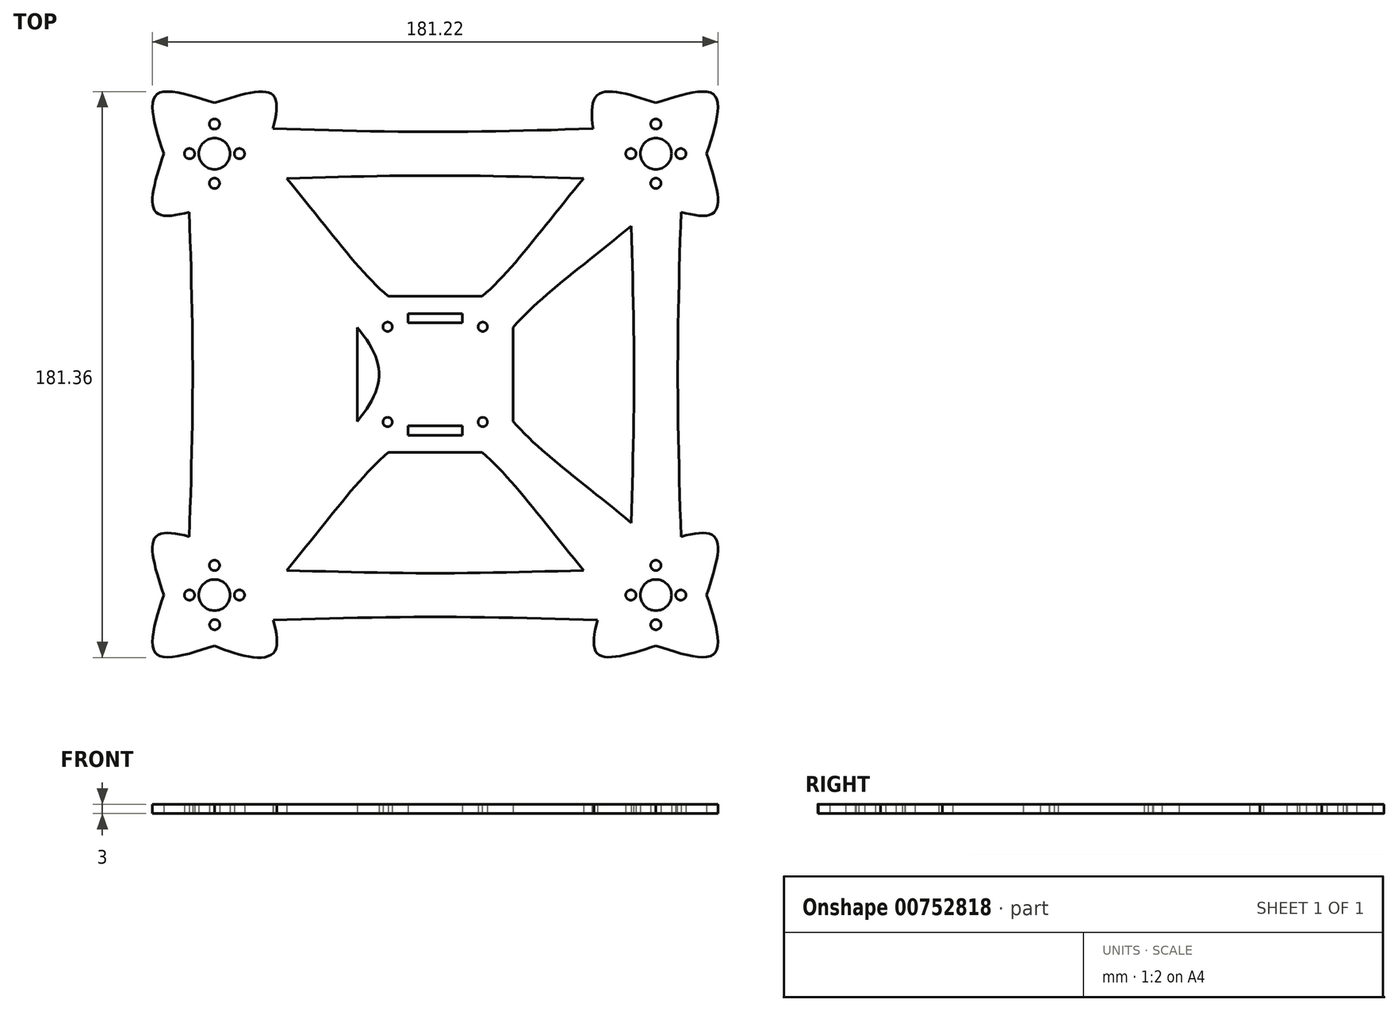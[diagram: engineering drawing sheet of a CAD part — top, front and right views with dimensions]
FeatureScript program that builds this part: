
annotation { "Feature Type Name" : "Feature", "Feature Type Description" : "" }
export const myFeature = defineFeature(function(context is Context, id is Id, definition is map)
    precondition{}
    {
        {
            var Q0;
            Q0=qCreatedBy(makeId("Top.planeOp"),FACE);
            var sketch = newSketch(context, id + "F0", { "sketchPlane" : qUnion([Q0])});
            skLineSegment(sketch, "E0.bottom", {"start": v(-18, 18) * mm, "end": v(18, 18) * mm, "construction": true});
            skLineSegment(sketch, "E0.top", {"start": v(-18, -18) * mm, "end": v(18, -18) * mm, "construction": true});
            skLineSegment(sketch, "E0.left", {"start": v(-18, 18) * mm, "end": v(-18, -18) * mm, "construction": true});
            skLineSegment(sketch, "E0.right", {"start": v(18, 18) * mm, "end": v(18, -18) * mm, "construction": true});
            skLineSegment(sketch, "E1", {"start": v(0, 18) * mm, "end": v(0, -18) * mm, "construction": true});
            skLineSegment(sketch, "E2", {"start": v(-18, 0) * mm, "end": v(18, 0) * mm, "construction": true});
            skPoint(sketch, "E3.positionSnap0", {"position": v(0, 0) * mm});
            skLineSegment(sketch, "E4", {"start": v(0, 0) * mm, "end": v(70.71, 70.71) * mm, "construction": true});
            skLineSegment(sketch, "E5", {"start": v(0, 0) * mm, "end": v(-70.71, -70.71) * mm, "construction": true});
            skLineSegment(sketch, "E6", {"start": v(0, 0) * mm, "end": v(70.71, -70.71) * mm, "construction": true});
            skCircle(sketch, "E7", {"center": v(-70.71, 70.71) * mm, "radius": 63.5 * mm, "construction": true});
            skCircle(sketch, "E8", {"center": v(70.71, 70.71) * mm, "radius": 63.5 * mm, "construction": true});
            skCircle(sketch, "E9", {"center": v(-70.71, -70.71) * mm, "radius": 63.5 * mm, "construction": true});
            skCircle(sketch, "E10", {"center": v(70.71, -70.71) * mm, "radius": 63.5 * mm, "construction": true});
            skCircle(sketch, "E11", {"center": v(-70.71, 70.71) * mm, "radius": 5 * mm});
            skCircle(sketch, "E12", {"center": v(70.71, 70.71) * mm, "radius": 5 * mm});
            skCircle(sketch, "E13", {"center": v(-70.71, -70.71) * mm, "radius": 5 * mm});
            skCircle(sketch, "E14", {"center": v(70.71, -70.71) * mm, "radius": 5 * mm});
            skLineSegment(sketch, "E15", {"start": v(-70.71, 70.71) * mm, "end": v(-62.71, 70.71) * mm, "construction": true});
            skCircle(sketch, "E16", {"center": v(-78.71, 70.71) * mm, "radius": 1.65 * mm});
            skCircle(sketch, "E17", {"center": v(-70.71, 80.21) * mm, "radius": 1.65 * mm});
            skCircle(sketch, "E18", {"center": v(-62.71, 70.71) * mm, "radius": 1.65 * mm});
            skCircle(sketch, "E19", {"center": v(-70.71, 61.21) * mm, "radius": 1.65 * mm});
            skLineSegment(sketch, "E20", {"start": v(70.71, 70.71) * mm, "end": v(62.71, 70.71) * mm, "construction": true});
            skLineSegment(sketch, "E21", {"start": v(70.71, 70.71) * mm, "end": v(78.71, 70.71) * mm, "construction": true});
            skLineSegment(sketch, "E22", {"start": v(70.71, 70.71) * mm, "end": v(70.71, 80.21) * mm, "construction": true});
            skLineSegment(sketch, "E23", {"start": v(70.71, 70.71) * mm, "end": v(70.71, 61.21) * mm, "construction": true});
            skCircle(sketch, "E24", {"center": v(62.71, 70.71) * mm, "radius": 1.65 * mm});
            skCircle(sketch, "E25", {"center": v(70.71, 80.21) * mm, "radius": 1.65 * mm});
            skCircle(sketch, "E26", {"center": v(70.71, 61.21) * mm, "radius": 1.65 * mm});
            skCircle(sketch, "E27", {"center": v(78.71, 70.71) * mm, "radius": 1.65 * mm});
            skLineSegment(sketch, "E28", {"start": v(-70.71, -70.71) * mm, "end": v(-78.71, -70.71) * mm, "construction": true});
            skLineSegment(sketch, "E29", {"start": v(-70.71, -70.71) * mm, "end": v(-62.71, -70.71) * mm, "construction": true});
            skLineSegment(sketch, "E30", {"start": v(-70.71, -70.71) * mm, "end": v(-70.71, -61.21) * mm, "construction": true});
            skLineSegment(sketch, "E31", {"start": v(-70.71, -70.71) * mm, "end": v(-70.64, -80.21) * mm, "construction": true});
            skCircle(sketch, "E32", {"center": v(-78.71, -70.71) * mm, "radius": 1.65 * mm});
            skCircle(sketch, "E33", {"center": v(-70.71, -61.21) * mm, "radius": 1.65 * mm});
            skCircle(sketch, "E34", {"center": v(-62.71, -70.71) * mm, "radius": 1.65 * mm});
            skCircle(sketch, "E35", {"center": v(-70.64, -80.21) * mm, "radius": 1.65 * mm});
            skLineSegment(sketch, "E36", {"start": v(70.71, -70.71) * mm, "end": v(78.71, -70.71) * mm, "construction": true});
            skLineSegment(sketch, "E37", {"start": v(70.71, -70.71) * mm, "end": v(62.71, -70.71) * mm, "construction": true});
            skCircle(sketch, "E38", {"center": v(62.71, -70.71) * mm, "radius": 1.65 * mm});
            skCircle(sketch, "E39", {"center": v(78.71, -70.71) * mm, "radius": 1.65 * mm});
            skLineSegment(sketch, "E40", {"start": v(70.71, -70.71) * mm, "end": v(70.71, -61.21) * mm, "construction": true});
            skLineSegment(sketch, "E41", {"start": v(70.71, -70.71) * mm, "end": v(70.71, -80.21) * mm, "construction": true});
            skCircle(sketch, "E42", {"center": v(70.71, -61.21) * mm, "radius": 1.65 * mm});
            skCircle(sketch, "E43", {"center": v(70.71, -80.21) * mm, "radius": 1.65 * mm});
            skCircle(sketch, "E44", {"center": v(-15.25, 15.25) * mm, "radius": 1.5 * mm});
            skCircle(sketch, "E45", {"center": v(15.25, 15.25) * mm, "radius": 1.5 * mm});
            skCircle(sketch, "E46", {"center": v(-15.25, -15.25) * mm, "radius": 1.5 * mm});
            skCircle(sketch, "E47", {"center": v(15.25, -15.25) * mm, "radius": 1.5 * mm});
            skLineSegment(sketch, "E48", {"start": v(-15.25, 15.25) * mm, "end": v(15.25, 15.25) * mm, "construction": true});
            skLineSegment(sketch, "E49", {"start": v(-15.25, 15.25) * mm, "end": v(-15.25, -15.25) * mm, "construction": true});
            skLineSegment(sketch, "E50", {"start": v(15.25, -15.25) * mm, "end": v(-15.25, -15.25) * mm, "construction": true});
            skLineSegment(sketch, "E51", {"start": v(15.25, 15.25) * mm, "end": v(15.25, -15.25) * mm, "construction": true});
            skCircle(sketch, "E52", {"center": v(-70.71, 70.71) * mm, "radius": 13.3 * mm, "construction": true});
            skLineSegment(sketch, "E53.bottom", {"start": v(-51.96, 89.46) * mm, "end": v(-89.46, 89.46) * mm, "construction": true});
            skLineSegment(sketch, "E53.top", {"start": v(-51.96, 51.96) * mm, "end": v(-89.46, 51.96) * mm, "construction": true});
            skLineSegment(sketch, "E53.left", {"start": v(-51.96, 89.46) * mm, "end": v(-51.96, 51.96) * mm, "construction": true});
            skLineSegment(sketch, "E53.right", {"start": v(-89.46, 89.46) * mm, "end": v(-89.46, 51.96) * mm, "construction": true});
            skLineSegment(sketch, "E54", {"start": v(-70.71, 84.01) * mm, "end": v(-70.71, 89.46) * mm, "construction": true});
            skLineSegment(sketch, "E55", {"start": v(-70.71, 89.46) * mm, "end": v(-89.46, 89.46) * mm, "construction": true});
            skLineSegment(sketch, "E56", {"start": v(-89.46, 70.71) * mm, "end": v(-89.46, 51.96) * mm, "construction": true});
            skLineSegment(sketch, "E57", {"start": v(-70.71, 51.96) * mm, "end": v(-51.96, 51.96) * mm, "construction": true});
            skLineSegment(sketch, "E58", {"start": v(-51.96, 70.71) * mm, "end": v(-51.96, 89.46) * mm, "construction": true});
            skLineSegment(sketch, "E59", {"start": v(-70.71, 89.46) * mm, "end": v(-51.96, 89.46) * mm, "construction": true});
            skLineSegment(sketch, "E60.0", {"start": v(-86.96, 86.96) * mm, "end": v(-86.96, 54.46) * mm, "construction": true});
            skLineSegment(sketch, "E60.1", {"start": v(-54.46, 86.96) * mm, "end": v(-86.96, 86.96) * mm, "construction": true});
            skLineSegment(sketch, "E60.2", {"start": v(-54.46, 86.96) * mm, "end": v(-54.46, 54.46) * mm, "construction": true});
            skLineSegment(sketch, "E60.3", {"start": v(-54.46, 54.46) * mm, "end": v(-86.96, 54.46) * mm, "construction": true});
            skFitSpline(sketch, "E61", {"points": [v(-70.71, 86.96) * mm, v(-89.46, 89.46) * mm, v(-86.96, 70.71) * mm], "startDerivative": vector(-48.13, 15.62) * mm, "endDerivative": vector(15.63, -48.13) * mm});
            skCircle(sketch, "E62", {"center": v(70.71, 70.71) * mm, "radius": 13.3 * mm, "construction": true});
            skLineSegment(sketch, "E63.bottom", {"start": v(89.46, 89.46) * mm, "end": v(51.96, 89.46) * mm, "construction": true});
            skLineSegment(sketch, "E63.top", {"start": v(89.46, 51.96) * mm, "end": v(51.96, 51.96) * mm, "construction": true});
            skLineSegment(sketch, "E63.left", {"start": v(89.46, 89.46) * mm, "end": v(89.46, 51.96) * mm, "construction": true});
            skLineSegment(sketch, "E63.right", {"start": v(51.96, 89.46) * mm, "end": v(51.96, 51.96) * mm, "construction": true});
            skLineSegment(sketch, "E64.bottom", {"start": v(86.96, 86.96) * mm, "end": v(54.46, 86.96) * mm, "construction": true});
            skLineSegment(sketch, "E64.top", {"start": v(86.96, 54.46) * mm, "end": v(54.46, 54.46) * mm, "construction": true});
            skLineSegment(sketch, "E64.left", {"start": v(86.96, 86.96) * mm, "end": v(86.96, 54.46) * mm, "construction": true});
            skLineSegment(sketch, "E64.right", {"start": v(54.46, 86.96) * mm, "end": v(54.46, 54.46) * mm, "construction": true});
            skFitSpline(sketch, "E65", {"points": [v(70.71, 86.96) * mm, v(89.46, 89.46) * mm, v(86.96, 70.71) * mm], "startDerivative": vector(48.12, 15.62) * mm, "endDerivative": vector(-15.62, -48.12) * mm});
            skLineSegment(sketch, "E66.bottom", {"start": v(-89.46, -51.96) * mm, "end": v(-51.96, -51.96) * mm, "construction": true});
            skLineSegment(sketch, "E66.top", {"start": v(-89.46, -89.46) * mm, "end": v(-51.96, -89.46) * mm, "construction": true});
            skLineSegment(sketch, "E66.left", {"start": v(-89.46, -51.96) * mm, "end": v(-89.46, -89.46) * mm, "construction": true});
            skLineSegment(sketch, "E66.right", {"start": v(-51.96, -51.96) * mm, "end": v(-51.96, -89.46) * mm, "construction": true});
            skLineSegment(sketch, "E67.bottom", {"start": v(-86.96, -54.46) * mm, "end": v(-54.46, -54.46) * mm, "construction": true});
            skLineSegment(sketch, "E67.top", {"start": v(-86.96, -86.96) * mm, "end": v(-54.46, -86.96) * mm, "construction": true});
            skLineSegment(sketch, "E67.left", {"start": v(-86.96, -54.46) * mm, "end": v(-86.96, -86.96) * mm, "construction": true});
            skLineSegment(sketch, "E67.right", {"start": v(-54.46, -54.46) * mm, "end": v(-54.46, -86.96) * mm, "construction": true});
            skFitSpline(sketch, "E68", {"points": [v(-86.96, -70.71) * mm, v(-89.46, -89.46) * mm, v(-70.71, -86.96) * mm], "startDerivative": vector(-15.62, -48.13) * mm, "endDerivative": vector(48.13, 15.63) * mm});
            skLineSegment(sketch, "E69.bottom", {"start": v(89.46, -51.96) * mm, "end": v(51.96, -51.96) * mm, "construction": true});
            skLineSegment(sketch, "E69.top", {"start": v(89.46, -89.46) * mm, "end": v(51.96, -89.46) * mm, "construction": true});
            skLineSegment(sketch, "E69.left", {"start": v(89.46, -51.96) * mm, "end": v(89.46, -89.46) * mm, "construction": true});
            skLineSegment(sketch, "E69.right", {"start": v(51.96, -51.96) * mm, "end": v(51.96, -89.46) * mm, "construction": true});
            skLineSegment(sketch, "E70.bottom", {"start": v(54.46, -54.46) * mm, "end": v(86.96, -54.46) * mm, "construction": true});
            skLineSegment(sketch, "E70.top", {"start": v(54.46, -86.96) * mm, "end": v(86.96, -86.96) * mm, "construction": true});
            skLineSegment(sketch, "E70.left", {"start": v(54.46, -54.46) * mm, "end": v(54.46, -86.96) * mm, "construction": true});
            skLineSegment(sketch, "E70.right", {"start": v(86.96, -54.46) * mm, "end": v(86.96, -86.96) * mm, "construction": true});
            skFitSpline(sketch, "E71", {"points": [v(70.71, -86.96) * mm, v(89.46, -89.46) * mm, v(86.96, -70.71) * mm], "startDerivative": vector(48.13, -15.62) * mm, "endDerivative": vector(-15.62, 48.12) * mm});
            skLineSegment(sketch, "E72", {"start": v(51.96, -51.96) * mm, "end": v(47.02, -56.9) * mm, "construction": true});
            skFitSpline(sketch, "E73", {"points": [v(-86.96, -70.71) * mm, v(-89.46, -51.96) * mm, v(-70.71, -54.46) * mm], "startDerivative": vector(-15.62, 48.12) * mm, "endDerivative": vector(48.12, -15.62) * mm});
            skFitSpline(sketch, "E74", {"points": [v(-70.71, -86.96) * mm, v(-51.96, -89.46) * mm, v(-54.46, -70.71) * mm], "startDerivative": vector(42, -18.12) * mm, "endDerivative": vector(-15.63, 48.12) * mm});
            skFitSpline(sketch, "E75", {"points": [v(86.96, -70.71) * mm, v(89.46, -51.96) * mm, v(70.71, -54.46) * mm], "startDerivative": vector(15.62, 48.13) * mm, "endDerivative": vector(-48.12, -15.62) * mm});
            skFitSpline(sketch, "E76", {"points": [v(70.71, -86.96) * mm, v(51.96, -89.46) * mm, v(54.46, -70.71) * mm], "startDerivative": vector(-48.13, -15.62) * mm, "endDerivative": vector(15.62, 48.12) * mm});
            skFitSpline(sketch, "E77", {"points": [v(86.96, 70.71) * mm, v(89.46, 51.96) * mm, v(70.71, 54.46) * mm], "startDerivative": vector(15.62, -48.13) * mm, "endDerivative": vector(-48.13, 15.62) * mm});
            skFitSpline(sketch, "E78", {"points": [v(70.71, 86.96) * mm, v(51.96, 89.46) * mm, v(51.96, 70.71) * mm], "startDerivative": vector(-46.8, 15.66) * mm, "endDerivative": vector(9.33, -48.2) * mm});
            skFitSpline(sketch, "E79", {"points": [v(-70.71, 86.96) * mm, v(-51.96, 89.46) * mm, v(-54.46, 70.71) * mm], "startDerivative": vector(48.13, 15.62) * mm, "endDerivative": vector(-15.62, -48.13) * mm});
            skFitSpline(sketch, "E80", {"points": [v(-86.96, 70.71) * mm, v(-89.46, 51.96) * mm, v(-70.71, 54.46) * mm], "startDerivative": vector(-15.62, -48.12) * mm, "endDerivative": vector(48.13, 15.62) * mm});
            skFitSpline(sketch, "E81", {"points": [v(-70.71, 54.46) * mm, v(-18, 0) * mm, v(-70.71, -54.46) * mm], "startDerivative": vector(141.82, -129.17) * mm, "endDerivative": vector(-141.82, -129.17) * mm});
            skFitSpline(sketch, "E82", {"points": [v(-54.46, 70.71) * mm, v(0, 18) * mm, v(54.46, 70.71) * mm], "startDerivative": vector(129.17, -141.82) * mm, "endDerivative": vector(129.17, 141.82) * mm});
            skFitSpline(sketch, "E83", {"points": [v(-54.46, -70.71) * mm, v(0, -18) * mm, v(54.46, -70.71) * mm], "startDerivative": vector(129.17, 141.82) * mm, "endDerivative": vector(129.16, -141.81) * mm});
            skFitSpline(sketch, "E84", {"points": [v(70.71, -54.46) * mm, v(18, 0) * mm, v(70.71, 54.46) * mm], "startDerivative": vector(-141.81, 129.16) * mm, "endDerivative": vector(141.82, 129.17) * mm});
            skLineSegment(sketch, "E85", {"start": v(-70.71, 54.46) * mm, "end": v(-86.96, 54.46) * mm, "construction": true});
            skLineSegment(sketch, "E86", {"start": v(-70.71, 54.46) * mm, "end": v(-54.46, 54.46) * mm, "construction": true});
            skLineSegment(sketch, "E87", {"start": v(-54.46, -54.46) * mm, "end": v(-70.71, -54.46) * mm, "construction": true});
            skLineSegment(sketch, "E88", {"start": v(-86.96, -54.46) * mm, "end": v(-70.71, -54.46) * mm, "construction": true});
            skLineSegment(sketch, "E89", {"start": v(-70.71, 54.46) * mm, "end": v(-70.71, -54.46) * mm, "construction": true});
            skLineSegment(sketch, "E90", {"start": v(-54.46, 70.71) * mm, "end": v(54.46, 70.71) * mm, "construction": true});
            skLineSegment(sketch, "E91", {"start": v(70.71, 54.46) * mm, "end": v(70.71, -54.46) * mm, "construction": true});
            skLineSegment(sketch, "E92", {"start": v(54.46, -70.71) * mm, "end": v(-54.46, -70.71) * mm, "construction": true});
            skPoint(sketch, "E93", {"position": v(-74.71, 88.24) * mm});
            skPoint(sketch, "E93.positionSnap0", {"position": v(-74.71, -70.71) * mm});
            skPoint(sketch, "E94", {"position": v(-70.71, 57.41) * mm});
            skPoint(sketch, "E94.positionSnap0", {"position": v(-70.71, 0) * mm});
            skPoint(sketch, "E95", {"position": v(0, 70.71) * mm});
            skPoint(sketch, "E96", {"position": v(70.71, 0) * mm});
            skPoint(sketch, "E97", {"position": v(0, -70.71) * mm});
            skLineSegment(sketch, "E98", {"start": v(-70.71, 0) * mm, "end": v(-77.71, 0) * mm, "construction": true});
            skLineSegment(sketch, "E99", {"start": v(-70.71, 0) * mm, "end": v(-63.71, 0) * mm, "construction": true});
            skLineSegment(sketch, "E100", {"start": v(0, -70.71) * mm, "end": v(0, 15.25) * mm, "construction": true});
            skLineSegment(sketch, "E101", {"start": v(0, -70.71) * mm, "end": v(0, -77.71) * mm, "construction": true});
            skLineSegment(sketch, "E102", {"start": v(0, -70.71) * mm, "end": v(0, -63.71) * mm, "construction": true});
            skLineSegment(sketch, "E103", {"start": v(70.71, 0) * mm, "end": v(63.71, 0) * mm, "construction": true});
            skLineSegment(sketch, "E104", {"start": v(70.71, 0) * mm, "end": v(77.71, 0) * mm, "construction": true});
            skLineSegment(sketch, "E105", {"start": v(0, 70.71) * mm, "end": v(0, 77.71) * mm, "construction": true});
            skLineSegment(sketch, "E106", {"start": v(0, 70.71) * mm, "end": v(0, 63.71) * mm, "construction": true});
            skLineSegment(sketch, "E107", {"start": v(-70.71, 54.46) * mm, "end": v(-54.46, 54.46) * mm});
            skLineSegment(sketch, "E108", {"start": v(-86.96, -54.46) * mm, "end": v(-70.71, -54.46) * mm});
            skLineSegment(sketch, "E109", {"start": v(-54.46, -54.46) * mm, "end": v(-70.71, -54.46) * mm});
            skPoint(sketch, "E110", {"position": v(-78.84, 54.46) * mm});
            skPoint(sketch, "E111", {"position": v(-62.59, 54.46) * mm});
            skPoint(sketch, "E112", {"position": v(-78.84, -54.46) * mm});
            skPoint(sketch, "E113", {"position": v(-62.59, -54.46) * mm});
            skFitSpline(sketch, "E114", {"points": [v(-78.84, 54.46) * mm, v(-77.71, 0) * mm, v(-78.84, -54.46) * mm], "startDerivative": vector(3.38, -108.92) * mm, "endDerivative": vector(-3.38, -108.92) * mm});
            skFitSpline(sketch, "E115", {"points": [v(-62.59, 54.46) * mm, v(-63.71, 0) * mm, v(-62.59, -54.46) * mm], "startDerivative": vector(-3.37, -108.92) * mm, "endDerivative": vector(3.38, -108.92) * mm});
            skLineSegment(sketch, "E116", {"start": v(-54.46, -54.46) * mm, "end": v(-54.46, -70.71) * mm, "construction": true});
            skLineSegment(sketch, "E117", {"start": v(-54.46, -86.96) * mm, "end": v(-54.46, -70.71) * mm, "construction": true});
            skLineSegment(sketch, "E118", {"start": v(54.46, -54.46) * mm, "end": v(54.46, -70.71) * mm, "construction": true});
            skLineSegment(sketch, "E119", {"start": v(54.46, -86.96) * mm, "end": v(54.46, -70.71) * mm, "construction": true});
            skPoint(sketch, "E120", {"position": v(-54.46, -62.59) * mm});
            skPoint(sketch, "E121", {"position": v(-54.46, -78.84) * mm});
            skPoint(sketch, "E122", {"position": v(54.46, -62.59) * mm});
            skPoint(sketch, "E123", {"position": v(54.46, -78.84) * mm});
            skLineSegment(sketch, "E124", {"start": v(54.46, -54.46) * mm, "end": v(70.71, -54.46) * mm, "construction": true});
            skLineSegment(sketch, "E125", {"start": v(86.96, -54.46) * mm, "end": v(70.71, -54.46) * mm, "construction": true});
            skLineSegment(sketch, "E126", {"start": v(86.96, 54.46) * mm, "end": v(70.71, 54.46) * mm, "construction": true});
            skLineSegment(sketch, "E127", {"start": v(54.46, 54.46) * mm, "end": v(70.71, 54.46) * mm, "construction": true});
            skFitSpline(sketch, "E128", {"points": [v(62.59, -54.46) * mm, v(63.71, 0) * mm, v(62.59, 54.46) * mm], "startDerivative": vector(3.37, 108.92) * mm, "endDerivative": vector(-3.38, 108.92) * mm});
            skFitSpline(sketch, "E129", {"points": [v(78.84, 54.46) * mm, v(77.71, 0) * mm, v(78.84, -54.46) * mm], "startDerivative": vector(-3.37, -108.92) * mm, "endDerivative": vector(3.38, -108.92) * mm});
            skFitSpline(sketch, "E130", {"points": [v(54.46, -62.59) * mm, v(0, -63.71) * mm, v(-54.46, -62.59) * mm], "startDerivative": vector(-108.92, -3.38) * mm, "endDerivative": vector(-108.92, 3.38) * mm});
            skFitSpline(sketch, "E131", {"points": [v(-54.46, -78.84) * mm, v(0, -77.71) * mm, v(54.46, -78.84) * mm], "startDerivative": vector(108.92, 3.37) * mm, "endDerivative": vector(108.92, -3.37) * mm});
            skLineSegment(sketch, "E132", {"start": v(-54.46, 86.96) * mm, "end": v(-54.46, 70.71) * mm, "construction": true});
            skLineSegment(sketch, "E133", {"start": v(-54.46, 54.46) * mm, "end": v(-54.46, 70.71) * mm, "construction": true});
            skLineSegment(sketch, "E134", {"start": v(54.46, 86.96) * mm, "end": v(54.46, 70.71) * mm, "construction": true});
            skLineSegment(sketch, "E135", {"start": v(54.46, 70.71) * mm, "end": v(54.46, 54.46) * mm, "construction": true});
            skFitSpline(sketch, "E136", {"points": [v(-54.46, 78.84) * mm, v(0, 77.71) * mm, v(54.46, 78.84) * mm], "startDerivative": vector(108.92, -3.37) * mm, "endDerivative": vector(108.92, 3.38) * mm});
            skPoint(sketch, "E137", {"position": v(-54.46, 62.59) * mm});
            skFitSpline(sketch, "E138", {"points": [v(54.46, 62.59) * mm, v(0, 63.71) * mm, v(-54.46, 62.59) * mm], "startDerivative": vector(-108.92, 3.37) * mm, "endDerivative": vector(-108.92, -3.37) * mm});
            skLineSegment(sketch, "E139.bottom", {"start": v(-25, -25) * mm, "end": v(25, -25) * mm});
            skLineSegment(sketch, "E139.top", {"start": v(-25, 25) * mm, "end": v(25, 25) * mm});
            skLineSegment(sketch, "E139.left", {"start": v(-25, -25) * mm, "end": v(-25, 25) * mm});
            skLineSegment(sketch, "E139.right", {"start": v(25, -25) * mm, "end": v(25, 25) * mm});
            skLineSegment(sketch, "E140.bottom", {"start": v(-8.75, -16.5) * mm, "end": v(8.75, -16.5) * mm});
            skLineSegment(sketch, "E140.top", {"start": v(-8.75, -19.5) * mm, "end": v(8.75, -19.5) * mm});
            skLineSegment(sketch, "E140.left", {"start": v(-8.75, -16.5) * mm, "end": v(-8.75, -19.5) * mm});
            skLineSegment(sketch, "E140.right", {"start": v(8.75, -16.5) * mm, "end": v(8.75, -19.5) * mm});
            skPoint(sketch, "E141.middle", {"position": v(0, 15.25) * mm});
            skPoint(sketch, "E142", {"position": v(7.21, 70.71) * mm});
            skPoint(sketch, "E143", {"position": v(-7.21, 70.71) * mm});
            skLineSegment(sketch, "E144.bottom", {"start": v(8.75, 16.5) * mm, "end": v(-8.75, 16.5) * mm});
            skLineSegment(sketch, "E144.top", {"start": v(8.75, 19.5) * mm, "end": v(-8.75, 19.5) * mm});
            skLineSegment(sketch, "E144.left", {"start": v(8.75, 16.5) * mm, "end": v(8.75, 19.5) * mm});
            skLineSegment(sketch, "E144.right", {"start": v(-8.75, 16.5) * mm, "end": v(-8.75, 19.5) * mm});
            skSolve(sketch);
        }
        {
            var Q0;
            {var subQ0=sQuery(id+"F0.wireOp",EDGE,"E81");var subQ1=sQuery(id+"F0.wireOp",EDGE,"E73");var subQ2=makeQuery(id+"F0.imprint","INTERSECT",VERTEX,{"derivedFrom":[subQ1,subQ0]});Q0=makeQuery(id+"F0.imprint","IMPRINT",FACE,{"disambiguationData":[TD([[makeQuery(id+"F0.imprint","IMPRINT",EDGE,{"disambiguationData":[TD([[subQ2,1.0]])],"derivedFrom":subQ1}),1.0]])]});}
            var Q1;
            Q1=makeQuery(id+"F0.imprint","IMPRINT",FACE,{"disambiguationData":[TD([[makeQuery(id+"F0.imprint","IMPRINT",EDGE,{"derivedFrom":sQuery(id+"F0.wireOp",EDGE,"E12")}),-1.0]])]});
            var Q2;
            Q2=makeQuery(id+"F0.imprint","IMPRINT",FACE,{"disambiguationData":[TD([[makeQuery(id+"F0.imprint","IMPRINT",EDGE,{"derivedFrom":sQuery(id+"F0.wireOp",EDGE,"E44")}),-1.0]])]});
            var Q3;
            {var subQ0=sQuery(id+"F0.wireOp",EDGE,"E83");var subQ1=sQuery(id+"F0.wireOp",EDGE,"E74");var subQ2=makeQuery(id+"F0.imprint","INTERSECT",VERTEX,{"derivedFrom":[subQ1,subQ0]});Q3=makeQuery(id+"F0.imprint","IMPRINT",FACE,{"disambiguationData":[TD([[makeQuery(id+"F0.imprint","IMPRINT",EDGE,{"disambiguationData":[TD([[subQ2,1.0]])],"derivedFrom":subQ1}),-1.0]])]});}
            var Q4;
            Q4=makeQuery(id+"F0.imprint","IMPRINT",FACE,{"disambiguationData":[TD([[makeQuery(id+"F0.imprint","IMPRINT",EDGE,{"derivedFrom":sQuery(id+"F0.wireOp",EDGE,"E14")}),-1.0]])]});
            var Q5;
            Q5=makeQuery(id+"F0.imprint","IMPRINT",FACE,{"disambiguationData":[TD([[makeQuery(id+"F0.imprint","IMPRINT",EDGE,{"derivedFrom":sQuery(id+"F0.wireOp",EDGE,"E13")}),-1.0]])]});
            var Q6;
            {var subQ0=sQuery(id+"F0.wireOp",EDGE,"E84");var subQ1=sQuery(id+"F0.wireOp",EDGE,"E75");var subQ2=makeQuery(id+"F0.imprint","INTERSECT",VERTEX,{"derivedFrom":[subQ1,subQ0]});Q6=makeQuery(id+"F0.imprint","IMPRINT",FACE,{"disambiguationData":[TD([[makeQuery(id+"F0.imprint","IMPRINT",EDGE,{"disambiguationData":[TD([[subQ2,1.0]])],"derivedFrom":subQ1}),-1.0]])]});}
            var Q7;
            Q7=makeQuery(id+"F0.imprint","IMPRINT",FACE,{"disambiguationData":[TD([[makeQuery(id+"F0.imprint","IMPRINT",EDGE,{"derivedFrom":sQuery(id+"F0.wireOp",EDGE,"E11")}),-1.0]])]});
            var Q8;
            {var subQ0=sQuery(id+"F0.wireOp",EDGE,"E108");var subQ3=sQuery(id+"F0.wireOp",EDGE,"E114");var subQ5=makeQuery(id+"F0.imprint","INTERSECT",VERTEX,{"derivedFrom":[subQ0,subQ3]});Q8=makeQuery(id+"F0.imprint","IMPRINT",FACE,{"disambiguationData":[TD([[makeQuery(id+"F0.imprint","IMPRINT",EDGE,{"disambiguationData":[TD([[subQ5,1.0]])],"derivedFrom":subQ3}),1.0]])]});}
            var Q9;
            {var subQ0=sQuery(id+"F0.wireOp",EDGE,"E109");var subQ3=sQuery(id+"F0.wireOp",EDGE,"E115");var subQ5=makeQuery(id+"F0.imprint","INTERSECT",VERTEX,{"derivedFrom":[subQ0,subQ3]});Q9=makeQuery(id+"F0.imprint","IMPRINT",FACE,{"disambiguationData":[TD([[makeQuery(id+"F0.imprint","IMPRINT",EDGE,{"disambiguationData":[TD([[subQ5,1.0]])],"derivedFrom":subQ3}),-1.0]])]});}
            var Q10;
            {var subQ0=sQuery(id+"F0.wireOp",EDGE,"E107");var subQ3=sQuery(id+"F0.wireOp",EDGE,"E115");var subQ5=makeQuery(id+"F0.imprint","INTERSECT",VERTEX,{"derivedFrom":[subQ0,subQ3]});Q10=makeQuery(id+"F0.imprint","IMPRINT",FACE,{"disambiguationData":[TD([[makeQuery(id+"F0.imprint","IMPRINT",EDGE,{"disambiguationData":[TD([[subQ5,-1.0]])],"derivedFrom":subQ3}),-1.0]])]});}
            var Q11;
            {var subQ0=sQuery(id+"F0.wireOp",EDGE,"E139.right");var subQ1=sQuery(id+"F0.wireOp",EDGE,"E84");var subQ2=makeQuery(id+"F0.imprint","INTERSECT",VERTEX,{"disambiguationData":[OD(0.0)],"derivedFrom":[subQ1,subQ0]});Q11=makeQuery(id+"F0.imprint","IMPRINT",FACE,{"disambiguationData":[TD([[makeQuery(id+"F0.imprint","IMPRINT",EDGE,{"disambiguationData":[TD([[subQ2,-1.0]])],"derivedFrom":subQ1}),-1.0]])]});}
            var Q12;
            {var subQ0=sQuery(id+"F0.wireOp",EDGE,"E139.bottom");var subQ1=sQuery(id+"F0.wireOp",EDGE,"E83");var subQ2=makeQuery(id+"F0.imprint","INTERSECT",VERTEX,{"disambiguationData":[OD(0.0)],"derivedFrom":[subQ1,subQ0]});Q12=makeQuery(id+"F0.imprint","IMPRINT",FACE,{"disambiguationData":[TD([[makeQuery(id+"F0.imprint","IMPRINT",EDGE,{"disambiguationData":[TD([[subQ2,-1.0]])],"derivedFrom":subQ1}),-1.0]])]});}
            var Q13;
            {var subQ0=sQuery(id+"F0.wireOp",EDGE,"E139.left");var subQ1=sQuery(id+"F0.wireOp",EDGE,"E81");var subQ2=makeQuery(id+"F0.imprint","INTERSECT",VERTEX,{"disambiguationData":[OD(0.0)],"derivedFrom":[subQ1,subQ0]});Q13=makeQuery(id+"F0.imprint","IMPRINT",FACE,{"disambiguationData":[TD([[makeQuery(id+"F0.imprint","IMPRINT",EDGE,{"disambiguationData":[TD([[subQ2,-1.0]])],"derivedFrom":subQ1}),-1.0]])]});}
            var Q14;
            {var subQ0=sQuery(id+"F0.wireOp",EDGE,"E139.top");var subQ1=sQuery(id+"F0.wireOp",EDGE,"E82");var subQ2=makeQuery(id+"F0.imprint","INTERSECT",VERTEX,{"disambiguationData":[OD(0.0)],"derivedFrom":[subQ1,subQ0]});Q14=makeQuery(id+"F0.imprint","IMPRINT",FACE,{"disambiguationData":[TD([[makeQuery(id+"F0.imprint","IMPRINT",EDGE,{"disambiguationData":[TD([[subQ2,-1.0]])],"derivedFrom":subQ1}),1.0]])]});}
            extrude(context, id + "F1", {"entities" : qUnion([Q0, Q1, Q2, Q3, Q4, Q5, Q6, Q7, Q8, Q9, Q10, Q11, Q12, Q13, Q14]), "depth" : 3 * mm, "offsetDistance" : 25 * mm});
        }
    });
